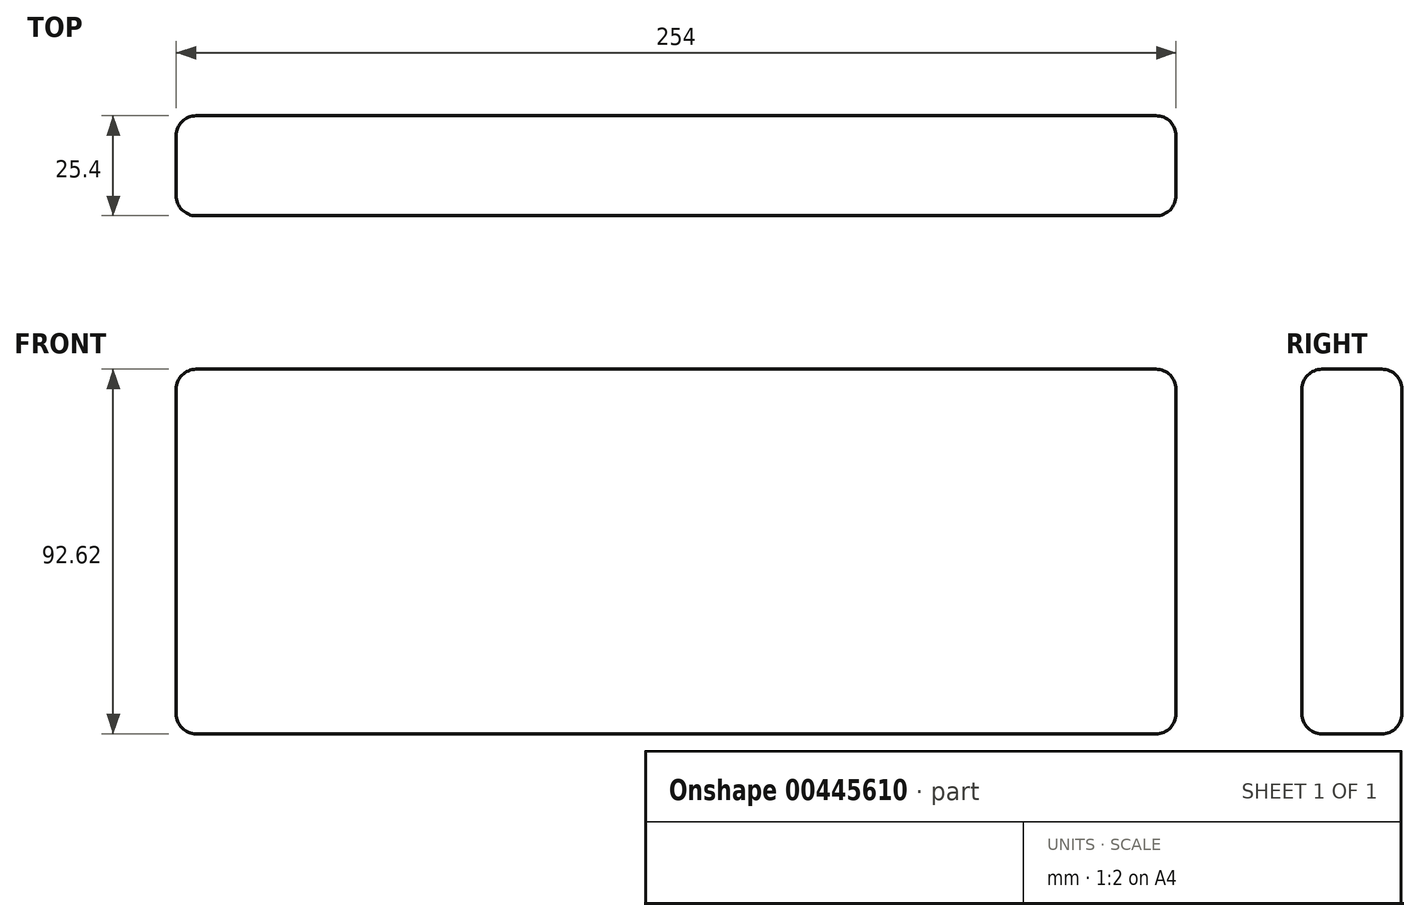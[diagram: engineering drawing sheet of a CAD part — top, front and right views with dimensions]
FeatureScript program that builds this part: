
annotation { "Feature Type Name" : "Feature", "Feature Type Description" : "" }
export const myFeature = defineFeature(function(context is Context, id is Id, definition is map)
    precondition{}
    {
        {
            var Q0;
            Q0=qCreatedBy(makeId("Front.planeOp"),FACE);
            var sketch = newSketch(context, id + "F0", { "sketchPlane" : qUnion([Q0])});
            skLineSegment(sketch, "E0.bottom", {"start": v(-127, -46.31) * mm, "end": v(127, -46.31) * mm});
            skLineSegment(sketch, "E0.top", {"start": v(-127, 46.31) * mm, "end": v(127, 46.31) * mm});
            skLineSegment(sketch, "E0.left", {"start": v(-127, -46.31) * mm, "end": v(-127, 46.31) * mm});
            skLineSegment(sketch, "E0.right", {"start": v(127, -46.31) * mm, "end": v(127, 46.31) * mm});
            skPoint(sketch, "E0.middle", {"position": v(0, 0) * mm});
            skSolve(sketch);
        }
        {
            var Q0;
            Q0 = qSketchRegion(id + "F0", true);
            extrude(context, id + "F1", {"entities" : qUnion([Q0]), "depth" : 25.4 * mm});
        }
        {
            var Q0;
            Q0=makeQuery(id+"F1.opExtrude","CAP_EDGE",EDGE,{"disambiguationData":[OSD([sQuery(id+"F0.wireOp",EDGE,"E0.top")])],"isStart":false});
            fillet(context, id + "F2", {"entities" : qUnion([Q0]), "radius" : 5.08 * mm, "tangentPropagation" : true, "allowEdgeOverflow" : false});
        }
        {
            var Q0;
            Q0=makeQuery(id+"F1.opExtrude","CAP_EDGE",EDGE,{"disambiguationData":[OSD([sQuery(id+"F0.wireOp",EDGE,"E0.top")])],"isStart":true});
            var Q1;
            Q1=makeQuery(id+"F1.opExtrude","SWEPT_EDGE",EDGE,{"disambiguationData":[OSD([sQuery(id+"F0.wireOp",EDGE,"E0.top"),sQuery(id+"F0.wireOp",EDGE,"E0.right")])]});
            var Q2;
            Q2=makeQuery(id+"F1.opExtrude","SWEPT_EDGE",EDGE,{"disambiguationData":[OSD([sQuery(id+"F0.wireOp",EDGE,"E0.top"),sQuery(id+"F0.wireOp",EDGE,"E0.left")])]});
            var Q3;
            {var subQ0=sQuery(id+"F0.wireOp",EDGE,"E0.top");Q3=makeQuery(id+"F2.opFillet","BLEND_EDGE",EDGE,{"blendedFrom":[makeQuery(id+"F1.opExtrude","CAP_EDGE",EDGE,{"disambiguationData":[OSD([subQ0])],"isStart":false}),makeQuery(id+"F1.opExtrude","SWEPT_FACE",FACE,{"disambiguationData":[OSD([subQ0])]})],"blendedInto":[makeQuery(id+"F1.opExtrude","SWEPT_FACE",FACE,{"disambiguationData":[OSD([subQ0])]})]});}
            fillet(context, id + "F3", {"entities" : qUnion([Q0, Q1, Q2, Q3]), "radius" : 5.08 * mm, "tangentPropagation" : true, "allowEdgeOverflow" : false});
        }
        {
            var Q0;
            Q0=makeQuery(id+"F1.opExtrude","CAP_EDGE",EDGE,{"disambiguationData":[OSD([sQuery(id+"F0.wireOp",EDGE,"E0.right")])],"isStart":true});
            var Q1;
            Q1=makeQuery(id+"F1.opExtrude","SWEPT_EDGE",EDGE,{"disambiguationData":[OSD([sQuery(id+"F0.wireOp",EDGE,"E0.bottom"),sQuery(id+"F0.wireOp",EDGE,"E0.right")])]});
            var Q2;
            Q2=makeQuery(id+"F1.opExtrude","CAP_EDGE",EDGE,{"disambiguationData":[OSD([sQuery(id+"F0.wireOp",EDGE,"E0.bottom")])],"isStart":true});
            var Q3;
            Q3=makeQuery(id+"F1.opExtrude","CAP_EDGE",EDGE,{"disambiguationData":[OSD([sQuery(id+"F0.wireOp",EDGE,"E0.bottom")])],"isStart":false});
            fillet(context, id + "F4", {"entities" : qUnion([Q0, Q1, Q2, Q3]), "radius" : 5.08 * mm, "tangentPropagation" : true, "allowEdgeOverflow" : false});
        }
        {
            var Q0;
            {var subQ0=sQuery(id+"F0.wireOp",EDGE,"E0.left");Q0=makeQuery(id+"F3.opFillet","BLEND_EDGE",EDGE,{"blendedFrom":[makeQuery(id+"F1.opExtrude","SWEPT_EDGE",EDGE,{"disambiguationData":[OSD([sQuery(id+"F0.wireOp",EDGE,"E0.top"),subQ0])]}),makeQuery(id+"F1.opExtrude","SWEPT_FACE",FACE,{"disambiguationData":[OSD([subQ0])]})],"blendedInto":[makeQuery(id+"F1.opExtrude","SWEPT_FACE",FACE,{"disambiguationData":[OSD([subQ0])]})]});}
            var Q1;
            Q1=makeQuery(id+"F1.opExtrude","CAP_EDGE",EDGE,{"disambiguationData":[OSD([sQuery(id+"F0.wireOp",EDGE,"E0.left")])],"isStart":true});
            var Q2;
            {var subQ0=sQuery(id+"F0.wireOp",EDGE,"E0.left");Q2=makeQuery(id+"F3.opFillet","BLEND_EDGE",EDGE,{"blendedFrom":[makeQuery(id+"F1.opExtrude","CAP_EDGE",EDGE,{"disambiguationData":[OSD([subQ0])],"isStart":false}),makeQuery(id+"F1.opExtrude","SWEPT_FACE",FACE,{"disambiguationData":[OSD([subQ0])]})],"blendedInto":[makeQuery(id+"F1.opExtrude","SWEPT_FACE",FACE,{"disambiguationData":[OSD([subQ0])]})]});}
            var Q3;
            {var subQ0=sQuery(id+"F0.wireOp",EDGE,"E0.left");Q3=makeQuery(id+"F4.opFillet","BLEND_EDGE",EDGE,{"blendedFrom":[makeQuery(id+"F1.opExtrude","SWEPT_EDGE",EDGE,{"disambiguationData":[OSD([sQuery(id+"F0.wireOp",EDGE,"E0.bottom"),subQ0])]}),makeQuery(id+"F1.opExtrude","SWEPT_FACE",FACE,{"disambiguationData":[OSD([subQ0])]})],"blendedInto":[makeQuery(id+"F1.opExtrude","SWEPT_FACE",FACE,{"disambiguationData":[OSD([subQ0])]})]});}
            var Q4;
            {var subQ0=sQuery(id+"F0.wireOp",EDGE,"E0.top");Q4=makeQuery(id+"F3.opFillet","BLEND_EDGE",EDGE,{"blendedFrom":[makeQuery(id+"F1.opExtrude","SWEPT_EDGE",EDGE,{"disambiguationData":[OSD([subQ0,sQuery(id+"F0.wireOp",EDGE,"E0.left")])]}),makeQuery(id+"F1.opExtrude","SWEPT_FACE",FACE,{"disambiguationData":[OSD([subQ0])]})],"blendedInto":[makeQuery(id+"F1.opExtrude","SWEPT_FACE",FACE,{"disambiguationData":[OSD([subQ0])]})]});}
            fillet(context, id + "F5", {"entities" : qUnion([Q0, Q1, Q2, Q3, Q4]), "radius" : 5.08 * mm, "tangentPropagation" : true, "allowEdgeOverflow" : false});
        }
    });
